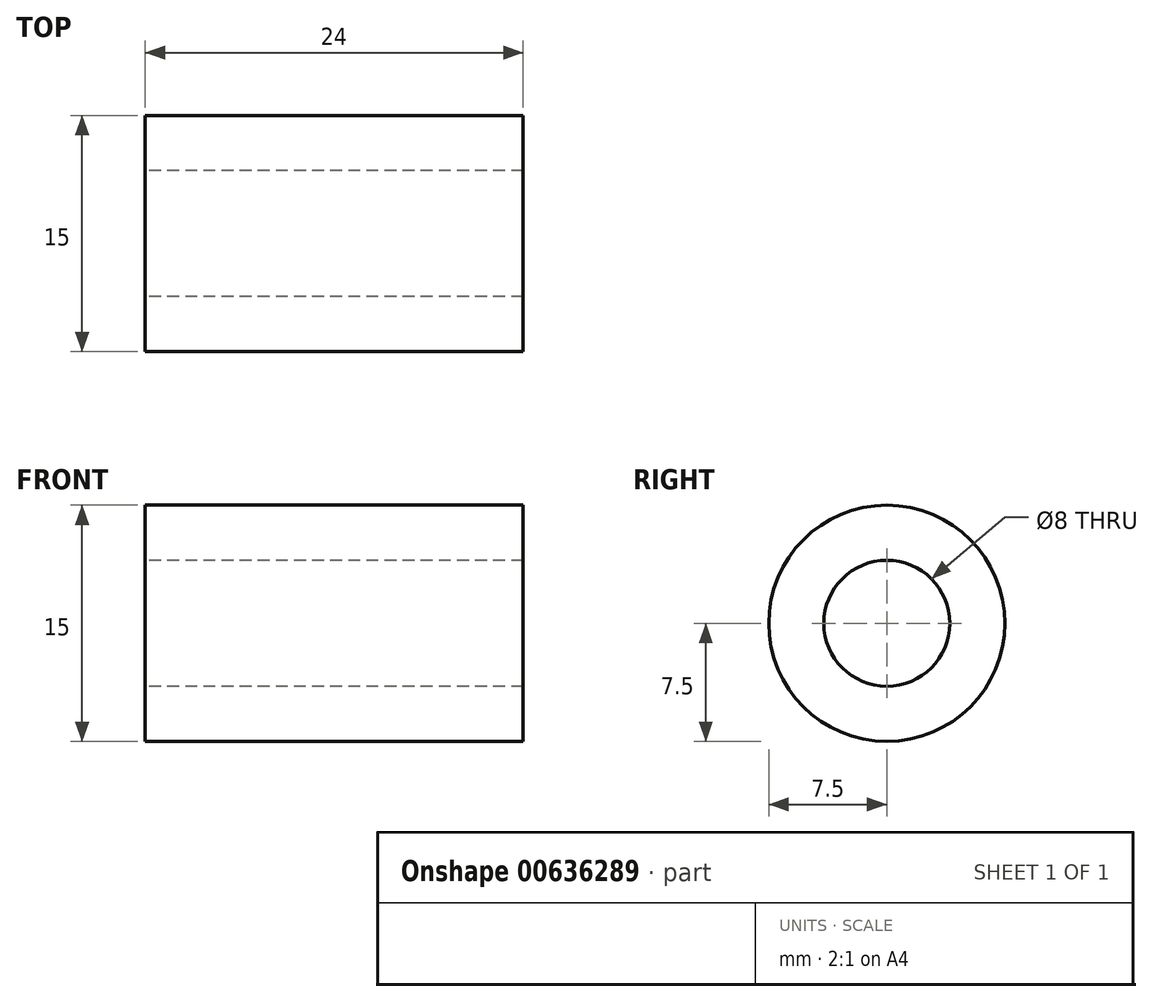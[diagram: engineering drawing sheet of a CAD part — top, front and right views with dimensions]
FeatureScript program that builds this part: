
annotation { "Feature Type Name" : "Feature", "Feature Type Description" : "" }
export const myFeature = defineFeature(function(context is Context, id is Id, definition is map)
    precondition{}
    {
        {
            var Q0;
            Q0=qCreatedBy(makeId("Right.planeOp"),FACE);
            var sketch = newSketch(context, id + "F0", { "sketchPlane" : qUnion([Q0])});
            skCircle(sketch, "E0", {"center": v(0, 0) * mm, "radius": 4 * mm});
            skCircle(sketch, "E1", {"center": v(0, 0) * mm, "radius": 7.5 * mm});
            skSolve(sketch);
        }
        {
            var Q0;
            Q0=qSketchRegion(id+"F0",true);
            extrude(context, id + "F1", {"entities" : qUnion([Q0]), "depth" : 24 * mm});
        }
    });
